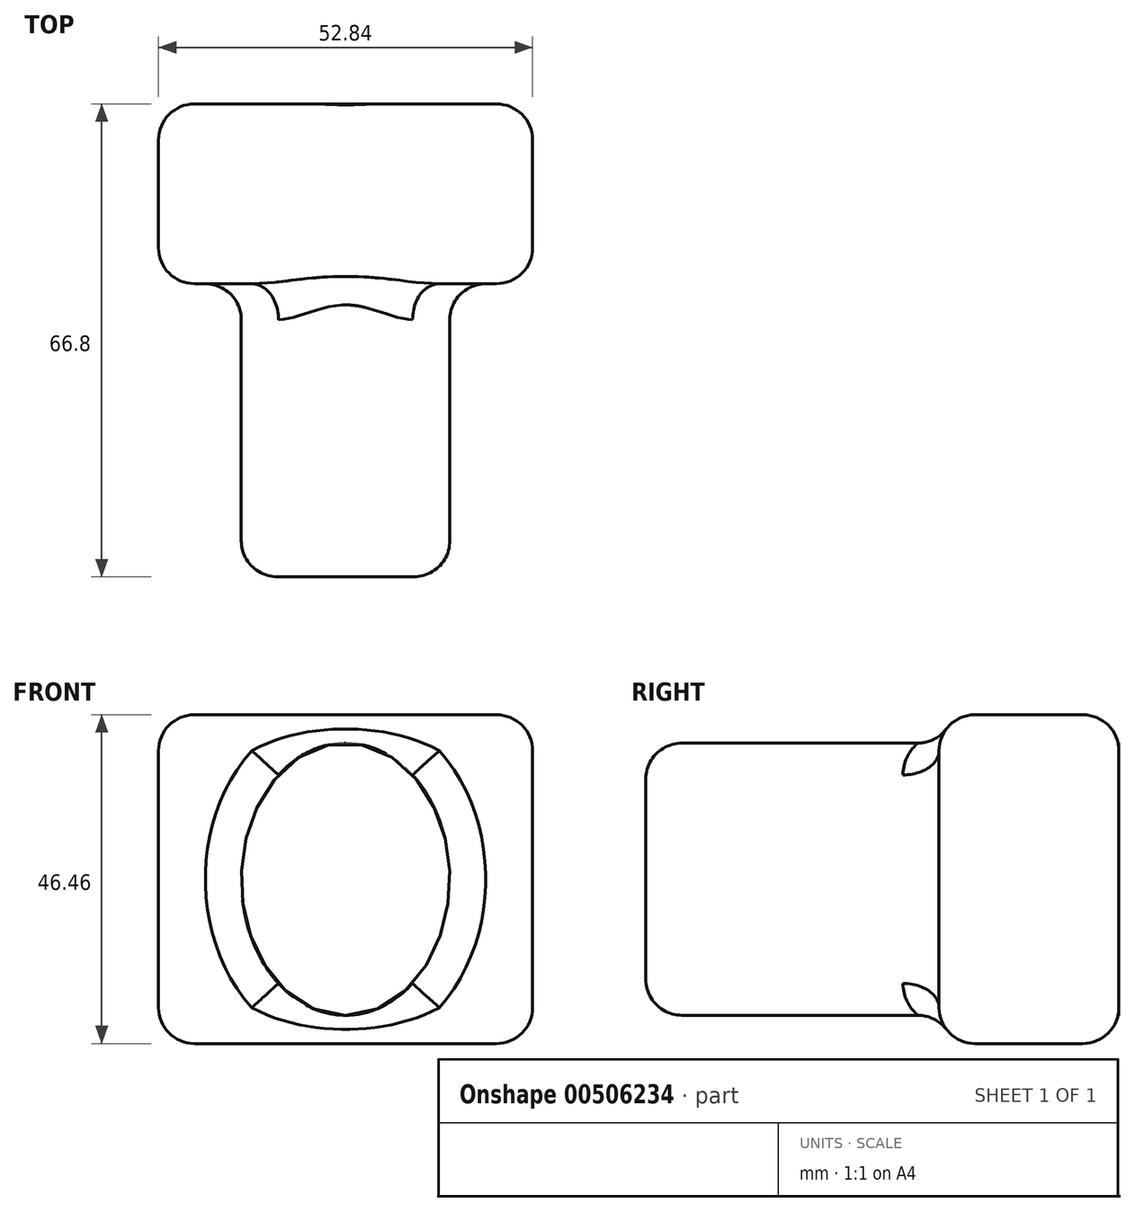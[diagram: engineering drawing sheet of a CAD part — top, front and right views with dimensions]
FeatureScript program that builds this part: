
annotation { "Feature Type Name" : "Feature", "Feature Type Description" : "" }
export const myFeature = defineFeature(function(context is Context, id is Id, definition is map)
    precondition{}
    {
        {
            var Q0;
            Q0=qCreatedBy(makeId("Front.planeOp"),FACE);
            var sketch = newSketch(context, id + "F0", { "sketchPlane" : qUnion([Q0])});
            skLineSegment(sketch, "E0.bottom", {"start": v(-26.42, 23.23) * mm, "end": v(26.42, 23.23) * mm});
            skLineSegment(sketch, "E0.top", {"start": v(-26.42, -23.23) * mm, "end": v(26.42, -23.23) * mm});
            skLineSegment(sketch, "E0.left", {"start": v(-26.42, 23.23) * mm, "end": v(-26.42, -23.23) * mm});
            skLineSegment(sketch, "E0.right", {"start": v(26.42, 23.23) * mm, "end": v(26.42, -23.23) * mm});
            skPoint(sketch, "E0.middle", {"position": v(0, 0) * mm});
            skLineSegment(sketch, "E1.bottom", {"start": v(-14.57, 9.87) * mm, "end": v(14.57, 9.87) * mm});
            skLineSegment(sketch, "E1.top", {"start": v(-14.57, -9.87) * mm, "end": v(14.57, -9.87) * mm});
            skLineSegment(sketch, "E1.left", {"start": v(-14.57, 9.87) * mm, "end": v(-14.57, -9.87) * mm});
            skLineSegment(sketch, "E1.right", {"start": v(14.57, 9.87) * mm, "end": v(14.57, -9.87) * mm});
            skSolve(sketch);
        }
        {
            var Q0;
            Q0 = qSketchRegion(id + "F0", true);
            extrude(context, id + "F1", {"entities" : qUnion([Q0]), "depth" : 25.4 * mm});
        }
        {
            var Q0;
            Q0=makeQuery(id+"F1.opExtrude","SWEPT_FACE",FACE,{"disambiguationData":[OSD([sQuery(id+"F0.wireOp",EDGE,"E0.top")])]});
            var Q1;
            Q1=makeQuery(id+"F1.opExtrude","SWEPT_FACE",FACE,{"disambiguationData":[OSD([sQuery(id+"F0.wireOp",EDGE,"E0.right")])]});
            var Q2;
            Q2=makeQuery(id+"F1.opExtrude","SWEPT_FACE",FACE,{"disambiguationData":[OSD([sQuery(id+"F0.wireOp",EDGE,"E0.bottom")])]});
            var Q3;
            Q3=makeQuery(id+"F1.opExtrude","SWEPT_FACE",FACE,{"disambiguationData":[OSD([sQuery(id+"F0.wireOp",EDGE,"E0.left")])]});
            fillet(context, id + "F2", {"entities" : qUnion([Q0, Q1, Q2, Q3]), "radius" : 5.08 * mm, "tangentPropagation" : true, "allowEdgeOverflow" : false});
        }
        {
            var Q0;
            Q0=qCreatedBy(makeId("Front.planeOp"),FACE);
            var sketch = newSketch(context, id + "F3", { "sketchPlane" : qUnion([Q0])});
            skEllipse(sketch, "E2", {"center": v(0, 0) * mm, "majorRadius": 14.73 * mm, "minorRadius": 19.23 * mm, "majorAxis": v(-1, 0)});
            skSolve(sketch);
        }
        {
            var Q0;
            Q0 = qSketchRegion(id + "F3", true);
            extrude(context, id + "F4", {"entities" : qUnion([Q0]), "operationType" : NewBodyOperationType.ADD, "depth" : 66.8 * mm});
        }
        {
            var Q0;
            Q0=makeQuery(id+"F4.opExtrude","CAP_FACE",FACE,{"disambiguationData":[OSD([sQuery(id+"F3.wireOp",EDGE,"E2")])],"isStart":false});
            fillet(context, id + "F5", {"entities" : qUnion([Q0]), "radius" : 5.08 * mm, "tangentPropagation" : true, "allowEdgeOverflow" : false});
        }
        {
            var Q0;
            {var subQ0=sQuery(id+"F0.wireOp",EDGE,"E1.left");var subQ1=sQuery(id+"F0.wireOp",EDGE,"E0.top");var subQ2=sQuery(id+"F0.wireOp",EDGE,"E0.left");var subQ3=sQuery(id+"F0.wireOp",EDGE,"E0.bottom");var subQ4=sQuery(id+"F0.wireOp",EDGE,"E1.top");var subQ5=sQuery(id+"F0.wireOp",EDGE,"E1.bottom");Q0=makeQuery(id+"F4.boolean.opBoolean","SPLIT",FACE,{"disambiguationData":[TD([makeQuery(id+"F1.opExtrude","SWEPT_FACE",FACE,{"disambiguationData":[OSD([subQ0])]})])],"derivedFrom":makeQuery(id+"F1.opExtrude","CAP_FACE",FACE,{"disambiguationData":[OSD([subQ3,subQ1,subQ2,sQuery(id+"F0.wireOp",EDGE,"E0.right"),subQ5,subQ4,subQ0,sQuery(id+"F0.wireOp",EDGE,"E1.right")])],"isStart":false})});}
            var Q1;
            {var subQ0=sQuery(id+"F0.wireOp",EDGE,"E0.right");var subQ1=sQuery(id+"F0.wireOp",EDGE,"E0.bottom");var subQ2=sQuery(id+"F0.wireOp",EDGE,"E1.top");var subQ3=sQuery(id+"F0.wireOp",EDGE,"E1.right");var subQ4=sQuery(id+"F0.wireOp",EDGE,"E1.bottom");var subQ5=sQuery(id+"F0.wireOp",EDGE,"E0.top");Q1=makeQuery(id+"F4.boolean.opBoolean","SPLIT",FACE,{"disambiguationData":[TD([makeQuery(id+"F1.opExtrude","SWEPT_FACE",FACE,{"disambiguationData":[OSD([subQ3])]})])],"derivedFrom":makeQuery(id+"F1.opExtrude","CAP_FACE",FACE,{"disambiguationData":[OSD([subQ1,subQ5,sQuery(id+"F0.wireOp",EDGE,"E0.left"),subQ0,subQ4,subQ2,sQuery(id+"F0.wireOp",EDGE,"E1.left"),subQ3])],"isStart":false})});}
            fillet(context, id + "F6", {"entities" : qUnion([Q0, Q1]), "radius" : 5.08 * mm, "tangentPropagation" : true, "allowEdgeOverflow" : false});
        }
    });
